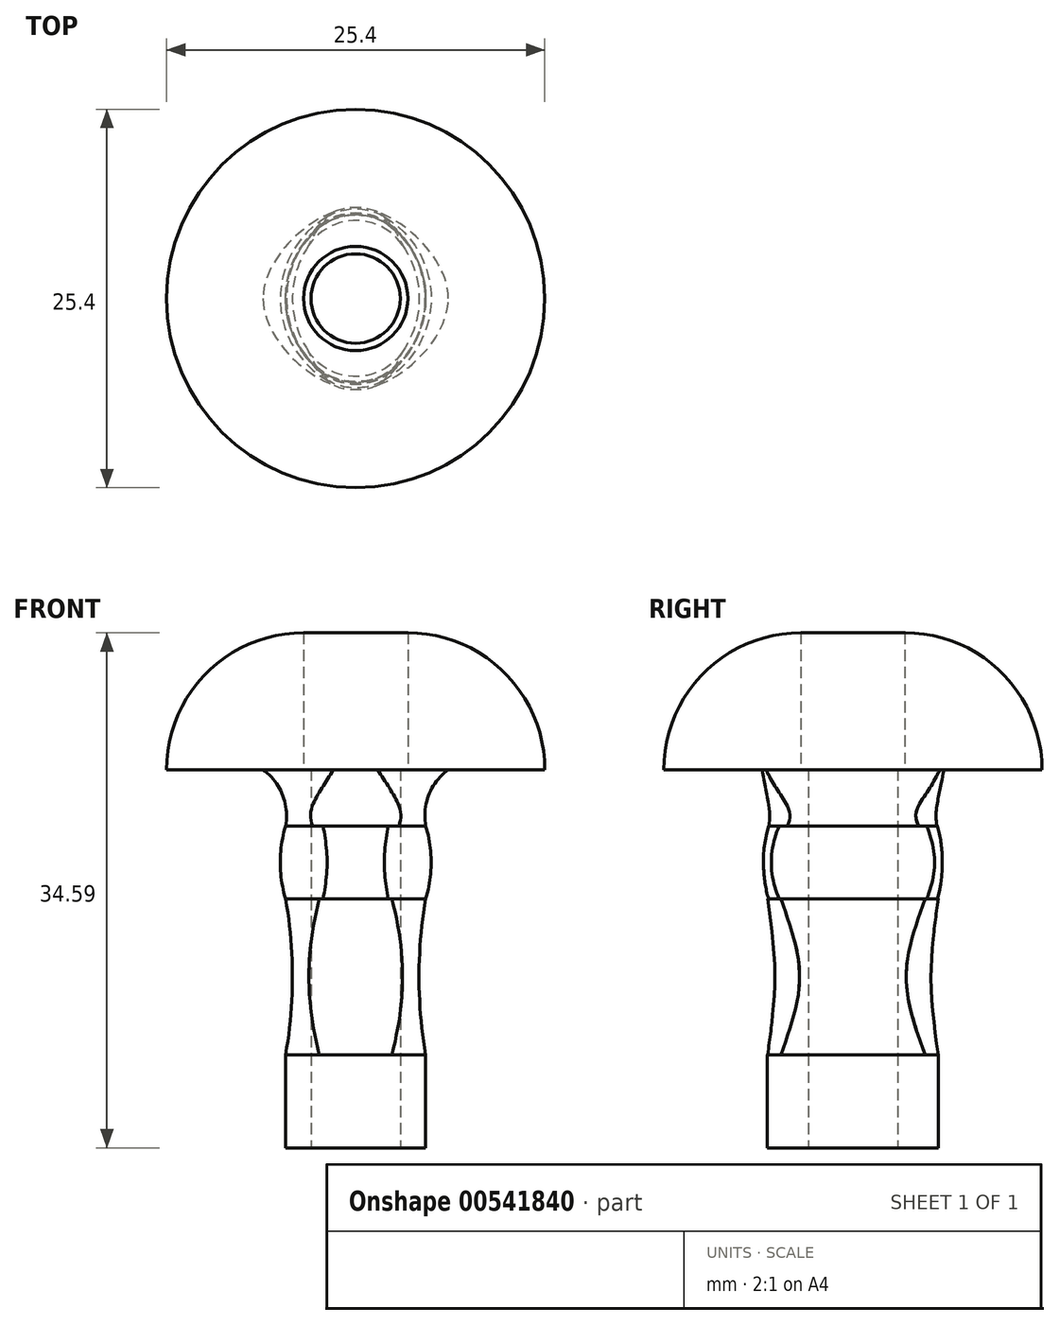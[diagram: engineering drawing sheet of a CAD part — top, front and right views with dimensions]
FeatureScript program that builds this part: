
annotation { "Feature Type Name" : "Feature", "Feature Type Description" : "" }
export const myFeature = defineFeature(function(context is Context, id is Id, definition is map)
    precondition{}
    {
        {
            var Q0;
            Q0=qCreatedBy(makeId("Front.planeOp"),FACE);
            var sketch = newSketch(context, id + "F0", { "sketchPlane" : qUnion([Q0])});
            skArc(sketch, "E0", {"start": v(-4.7, 21.62) * mm, "mid": v(-4.92, 23.73) * mm, "end": v(-6.22, 25.4) * mm});
            skArc(sketch, "E1", {"start": v(-4.7, 21.62) * mm, "mid": v(-5.07, 19.17) * mm, "end": v(-4.7, 16.71) * mm});
            skArc(sketch, "E2", {"start": v(-4.7, 6.26) * mm, "mid": v(-4.25, 11.49) * mm, "end": v(-4.7, 16.71) * mm});
            skLineSegment(sketch, "E3", {"start": v(-4.7, 6.26) * mm, "end": v(-3.92, 6.26) * mm});
            skLineSegment(sketch, "E4.MirrorCS", {"start": v(4.7, 6.26) * mm, "end": v(3.92, 6.26) * mm});
            skArc(sketch, "E5.MirrorCS", {"start": v(4.7, 6.26) * mm, "mid": v(4.25, 11.49) * mm, "end": v(4.7, 16.71) * mm});
            skArc(sketch, "E6.MirrorCS", {"start": v(4.7, 21.62) * mm, "mid": v(5.07, 19.17) * mm, "end": v(4.7, 16.71) * mm});
            skArc(sketch, "E7.MirrorCS", {"start": v(4.7, 21.62) * mm, "mid": v(4.92, 23.73) * mm, "end": v(6.22, 25.4) * mm});
            skLineSegment(sketch, "E8", {"start": v(-6.22, 25.4) * mm, "end": v(6.22, 25.4) * mm});
            skLineSegment(sketch, "E9", {"start": v(-4.7, 21.62) * mm, "end": v(4.7, 21.62) * mm});
            skLineSegment(sketch, "E10", {"start": v(-4.7, 16.71) * mm, "end": v(4.7, 16.71) * mm});
            skLineSegment(sketch, "E11", {"start": v(-3.92, 6.26) * mm, "end": v(3.92, 6.26) * mm});
            skLineSegment(sketch, "E12", {"start": v(-4.7, 6.26) * mm, "end": v(-4.7, 0) * mm});
            skLineSegment(sketch, "E13", {"start": v(-4.7, 0) * mm, "end": v(3.39, 0) * mm});
            skLineSegment(sketch, "E14", {"start": v(4.7, 6.26) * mm, "end": v(4.7, 0) * mm});
            skLineSegment(sketch, "E15", {"start": v(4.7, 0) * mm, "end": v(3.39, 0) * mm});
            skSolve(sketch);
        }
        {
            var Q0;
            Q0=qCreatedBy(makeId("Top.planeOp"),FACE);
            var sketch = newSketch(context, id + "F1", { "sketchPlane" : qUnion([Q0])});
            skCircle(sketch, "E16", {"center": v(0, 0) * mm, "radius": 3.5 * mm});
            skCircle(sketch, "E17", {"center": v(0, 0) * mm, "radius": 12.7 * mm});
            skSolve(sketch);
        }
        {
            var Q0;
            Q0=makeQuery(id+"F1.imprint","IMPRINT",FACE,{"disambiguationData":[TD([[makeQuery(id+"F1.imprint","IMPRINT",EDGE,{"derivedFrom":sQuery(id+"F1.wireOp",EDGE,"E16")}),-1.0]])]});
            extrude(context, id + "F2", {"entities" : qUnion([Q0]), "depth" : 9.2 * mm, "offsetDistance" : 25.4 * mm});
        }
        {
            var Q0;
            Q0=makeQuery(id+"F2.opExtrude","SWEPT_BODY",BODY,{"disambiguationData":[OSD([sQuery(id+"F1.wireOp",EDGE,"E16"),sQuery(id+"F1.wireOp",EDGE,"PXPxztUf-wTVu-soCt-rwad-Ievf1r8iTORp.bottom"),sQuery(id+"F1.wireOp",EDGE,"PXPxztUf-wTVu-soCt-rwad-Ievf1r8iTORp.top"),sQuery(id+"F1.wireOp",EDGE,"PXPxztUf-wTVu-soCt-rwad-Ievf1r8iTORp.left"),sQuery(id+"F1.wireOp",EDGE,"PXPxztUf-wTVu-soCt-rwad-Ievf1r8iTORp.right")])]});
            transform(context, id + "F3", {"entities" : qUnion([Q0]), "transformType" : TransformType.TRANSLATION_3D, "dx" : 0 * mm, "dy" : 0 * mm, "dz" : 25.4 * mm, "makeCopy" : false});
        }
        {
            var Q0;
            Q0=makeQuery(id+"F2.opExtrude","CAP_EDGE",EDGE,{"disambiguationData":[OSD([sQuery(id+"F1.wireOp",EDGE,"E17")])],"isStart":false});
            fillet(context, id + "F4", {"entities" : qUnion([Q0]), "radius" : 9.2 * mm, "tangentPropagation" : true, "allowEdgeOverflow" : false});
        }
        {
            var Q0;
            Q0=makeQuery(id+"F0.imprint","IMPRINT",FACE,{"disambiguationData":[TD([[makeQuery(id+"F0.imprint","IMPRINT",EDGE,{"derivedFrom":sQuery(id+"F0.wireOp",EDGE,"E2")}),-1.0]])]});
            extrude(context, id + "F5", {"entities" : qUnion([Q0]), "depth" : 12.7 * mm, "offsetDistance" : 25.4 * mm});
        }
        {
            var Q0;
            Q0=makeQuery(id+"F5.opExtrude","SWEPT_BODY",BODY,{"disambiguationData":[OSD([sQuery(id+"F0.wireOp",EDGE,"E2"),sQuery(id+"F0.wireOp",EDGE,"E3"),sQuery(id+"F0.wireOp",EDGE,"E4.MirrorCS"),sQuery(id+"F0.wireOp",EDGE,"E5.MirrorCS"),sQuery(id+"F0.wireOp",EDGE,"E10"),sQuery(id+"F0.wireOp",EDGE,"E11")])]});
            transform(context, id + "F6", {"entities" : qUnion([Q0]), "transformType" : TransformType.TRANSLATION_3D, "dx" : 0 * mm, "dy" : 6.35 * mm, "dz" : 0 * mm, "makeCopy" : false});
        }
        {
            var Q0;
            Q0=makeQuery(id+"F5.opExtrude","CAP_EDGE",EDGE,{"disambiguationData":[OSD([sQuery(id+"F0.wireOp",EDGE,"E5.MirrorCS")])],"isStart":false});
            var Q1;
            Q1=makeQuery(id+"F5.opExtrude","CAP_EDGE",EDGE,{"disambiguationData":[OSD([sQuery(id+"F0.wireOp",EDGE,"E2")])],"isStart":false});
            var Q2;
            Q2=makeQuery(id+"F5.opExtrude","CAP_EDGE",EDGE,{"disambiguationData":[OSD([sQuery(id+"F0.wireOp",EDGE,"E5.MirrorCS")])],"isStart":true});
            var Q3;
            Q3=makeQuery(id+"F5.opExtrude","CAP_EDGE",EDGE,{"disambiguationData":[OSD([sQuery(id+"F0.wireOp",EDGE,"E2")])],"isStart":true});
            fillet(context, id + "F7", {"entities" : qUnion([Q0, Q1, Q2, Q3]), "radius" : 6.35 * mm, "tangentPropagation" : true, "allowEdgeOverflow" : false});
        }
        {
            var Q0;
            Q0=makeQuery(id+"F0.imprint","IMPRINT",FACE,{"disambiguationData":[TD([[makeQuery(id+"F0.imprint","IMPRINT",EDGE,{"derivedFrom":sQuery(id+"F0.wireOp",EDGE,"E3")}),-1.0]])]});
            extrude(context, id + "F8", {"entities" : qUnion([Q0]), "depth" : 12.7 * mm, "offsetDistance" : 25.4 * mm});
        }
        {
            var Q0;
            Q0=makeQuery(id+"F8.opExtrude","SWEPT_BODY",BODY,{"disambiguationData":[OSD([sQuery(id+"F0.wireOp",EDGE,"E3"),sQuery(id+"F0.wireOp",EDGE,"E4.MirrorCS"),sQuery(id+"F0.wireOp",EDGE,"E11"),sQuery(id+"F0.wireOp",EDGE,"E12"),sQuery(id+"F0.wireOp",EDGE,"E13"),sQuery(id+"F0.wireOp",EDGE,"E14"),sQuery(id+"F0.wireOp",EDGE,"E15")])]});
            transform(context, id + "F9", {"entities" : qUnion([Q0]), "transformType" : TransformType.TRANSLATION_3D, "dx" : 0 * mm, "dy" : 6.35 * mm, "dz" : 0 * mm, "makeCopy" : false});
        }
        {
            var Q0;
            Q0=makeQuery(id+"F8.opExtrude","CAP_EDGE",EDGE,{"disambiguationData":[OSD([sQuery(id+"F0.wireOp",EDGE,"E14")])],"isStart":false});
            var Q1;
            Q1=makeQuery(id+"F8.opExtrude","CAP_EDGE",EDGE,{"disambiguationData":[OSD([sQuery(id+"F0.wireOp",EDGE,"E12")])],"isStart":false});
            var Q2;
            Q2=makeQuery(id+"F8.opExtrude","CAP_EDGE",EDGE,{"disambiguationData":[OSD([sQuery(id+"F0.wireOp",EDGE,"E14")])],"isStart":true});
            var Q3;
            Q3=makeQuery(id+"F8.opExtrude","CAP_EDGE",EDGE,{"disambiguationData":[OSD([sQuery(id+"F0.wireOp",EDGE,"E12")])],"isStart":true});
            fillet(context, id + "F10", {"entities" : qUnion([Q0, Q1, Q2, Q3]), "radius" : 6.35 * mm, "tangentPropagation" : true, "allowEdgeOverflow" : false});
        }
        {
            var Q0;
            Q0=makeQuery(id+"F0.imprint","IMPRINT",FACE,{"disambiguationData":[TD([[makeQuery(id+"F0.imprint","IMPRINT",EDGE,{"derivedFrom":sQuery(id+"F0.wireOp",EDGE,"E1")}),1.0]])]});
            extrude(context, id + "F11", {"entities" : qUnion([Q0]), "depth" : 12.7 * mm, "offsetDistance" : 25.4 * mm});
        }
        {
            var Q0;
            Q0=makeQuery(id+"F11.opExtrude","SWEPT_BODY",BODY,{"disambiguationData":[OSD([sQuery(id+"F0.wireOp",EDGE,"E1"),sQuery(id+"F0.wireOp",EDGE,"E6.MirrorCS"),sQuery(id+"F0.wireOp",EDGE,"E9"),sQuery(id+"F0.wireOp",EDGE,"E10")])]});
            transform(context, id + "F12", {"entities" : qUnion([Q0]), "transformType" : TransformType.TRANSLATION_3D, "dx" : 0 * mm, "dy" : 6.35 * mm, "dz" : 0 * mm, "makeCopy" : false});
        }
        {
            var Q0;
            Q0=makeQuery(id+"F11.opExtrude","CAP_EDGE",EDGE,{"disambiguationData":[OSD([sQuery(id+"F0.wireOp",EDGE,"E6.MirrorCS")])],"isStart":false});
            var Q1;
            Q1=makeQuery(id+"F11.opExtrude","CAP_EDGE",EDGE,{"disambiguationData":[OSD([sQuery(id+"F0.wireOp",EDGE,"E1")])],"isStart":false});
            var Q2;
            Q2=makeQuery(id+"F11.opExtrude","CAP_EDGE",EDGE,{"disambiguationData":[OSD([sQuery(id+"F0.wireOp",EDGE,"E6.MirrorCS")])],"isStart":true});
            var Q3;
            Q3=makeQuery(id+"F11.opExtrude","CAP_EDGE",EDGE,{"disambiguationData":[OSD([sQuery(id+"F0.wireOp",EDGE,"E1")])],"isStart":true});
            fillet(context, id + "F13", {"entities" : qUnion([Q0, Q1, Q2, Q3]), "radius" : 6.35 * mm, "tangentPropagation" : true, "allowEdgeOverflow" : false});
        }
        {
            var Q0;
            Q0=makeQuery(id+"F0.imprint","IMPRINT",FACE,{"disambiguationData":[TD([[makeQuery(id+"F0.imprint","IMPRINT",EDGE,{"derivedFrom":sQuery(id+"F0.wireOp",EDGE,"E0")}),-1.0]])]});
            extrude(context, id + "F14", {"entities" : qUnion([Q0]), "depth" : 12.7 * mm, "offsetDistance" : 25.4 * mm});
        }
        {
            var Q0;
            Q0=makeQuery(id+"F14.opExtrude","SWEPT_BODY",BODY,{"disambiguationData":[OSD([sQuery(id+"F0.wireOp",EDGE,"E0"),sQuery(id+"F0.wireOp",EDGE,"E7.MirrorCS"),sQuery(id+"F0.wireOp",EDGE,"E8"),sQuery(id+"F0.wireOp",EDGE,"E9")])]});
            transform(context, id + "F15", {"entities" : qUnion([Q0]), "transformType" : TransformType.TRANSLATION_3D, "dx" : 0 * mm, "dy" : 6.35 * mm, "dz" : 0 * mm, "makeCopy" : false});
        }
        {
            var Q0;
            Q0=makeQuery(id+"F14.opExtrude","CAP_EDGE",EDGE,{"disambiguationData":[OSD([sQuery(id+"F0.wireOp",EDGE,"E0")])],"isStart":false});
            var Q1;
            Q1=makeQuery(id+"F14.opExtrude","CAP_EDGE",EDGE,{"disambiguationData":[OSD([sQuery(id+"F0.wireOp",EDGE,"E7.MirrorCS")])],"isStart":false});
            var Q2;
            Q2=makeQuery(id+"F14.opExtrude","CAP_EDGE",EDGE,{"disambiguationData":[OSD([sQuery(id+"F0.wireOp",EDGE,"E7.MirrorCS")])],"isStart":true});
            var Q3;
            Q3=makeQuery(id+"F14.opExtrude","CAP_EDGE",EDGE,{"disambiguationData":[OSD([sQuery(id+"F0.wireOp",EDGE,"E0")])],"isStart":true});
            fillet(context, id + "F16", {"entities" : qUnion([Q0, Q1, Q2, Q3]), "radius" : 6.35 * mm, "tangentPropagation" : true, "allowEdgeOverflow" : false});
        }
        {
            var Q0;
            Q0=makeQuery(id+"F7.opFillet","BLEND_EDGE",EDGE,{"blendedFrom":[makeQuery(id+"F5.opExtrude","CAP_EDGE",EDGE,{"disambiguationData":[OSD([sQuery(id+"F0.wireOp",EDGE,"E2")])],"isStart":false}),makeQuery(id+"F5.opExtrude","CAP_EDGE",EDGE,{"disambiguationData":[OSD([sQuery(id+"F0.wireOp",EDGE,"E5.MirrorCS")])],"isStart":false})],"blendedInto":[]});
            var Q1;
            Q1=makeQuery(id+"F7.opFillet","BLEND_EDGE",EDGE,{"blendedFrom":[makeQuery(id+"F5.opExtrude","CAP_EDGE",EDGE,{"disambiguationData":[OSD([sQuery(id+"F0.wireOp",EDGE,"E2")])],"isStart":true}),makeQuery(id+"F5.opExtrude","CAP_EDGE",EDGE,{"disambiguationData":[OSD([sQuery(id+"F0.wireOp",EDGE,"E5.MirrorCS")])],"isStart":true})],"blendedInto":[]});
            fillet(context, id + "F17", {"entities" : qUnion([Q0, Q1]), "radius" : 3.8 * mm, "tangentPropagation" : true, "allowEdgeOverflow" : false});
        }
        {
            var Q0;
            Q0=makeQuery(id+"F10.opFillet","BLEND_EDGE",EDGE,{"blendedFrom":[makeQuery(id+"F8.opExtrude","CAP_EDGE",EDGE,{"disambiguationData":[OSD([sQuery(id+"F0.wireOp",EDGE,"E12")])],"isStart":false}),makeQuery(id+"F8.opExtrude","CAP_EDGE",EDGE,{"disambiguationData":[OSD([sQuery(id+"F0.wireOp",EDGE,"E14")])],"isStart":false})],"blendedInto":[]});
            var Q1;
            Q1=makeQuery(id+"F10.opFillet","BLEND_EDGE",EDGE,{"blendedFrom":[makeQuery(id+"F8.opExtrude","CAP_EDGE",EDGE,{"disambiguationData":[OSD([sQuery(id+"F0.wireOp",EDGE,"E12")])],"isStart":true}),makeQuery(id+"F8.opExtrude","CAP_EDGE",EDGE,{"disambiguationData":[OSD([sQuery(id+"F0.wireOp",EDGE,"E14")])],"isStart":true})],"blendedInto":[]});
            fillet(context, id + "F18", {"entities" : qUnion([Q0, Q1]), "radius" : 3.8 * mm, "tangentPropagation" : true, "allowEdgeOverflow" : false});
        }
        {
            var Q0;
            Q0=makeQuery(id+"F13.opFillet","BLEND_EDGE",EDGE,{"blendedFrom":[makeQuery(id+"F11.opExtrude","CAP_EDGE",EDGE,{"disambiguationData":[OSD([sQuery(id+"F0.wireOp",EDGE,"E1")])],"isStart":false}),makeQuery(id+"F11.opExtrude","CAP_EDGE",EDGE,{"disambiguationData":[OSD([sQuery(id+"F0.wireOp",EDGE,"E6.MirrorCS")])],"isStart":false})],"blendedInto":[]});
            var Q1;
            Q1=makeQuery(id+"F13.opFillet","BLEND_EDGE",EDGE,{"blendedFrom":[makeQuery(id+"F11.opExtrude","CAP_EDGE",EDGE,{"disambiguationData":[OSD([sQuery(id+"F0.wireOp",EDGE,"E1")])],"isStart":true}),makeQuery(id+"F11.opExtrude","CAP_EDGE",EDGE,{"disambiguationData":[OSD([sQuery(id+"F0.wireOp",EDGE,"E6.MirrorCS")])],"isStart":true})],"blendedInto":[]});
            fillet(context, id + "F19", {"entities" : qUnion([Q0, Q1]), "radius" : 3.8 * mm, "tangentPropagation" : true, "allowEdgeOverflow" : false});
        }
        {
            var Q0;
            Q0=makeQuery(id+"F16.opFillet","BLEND_EDGE",EDGE,{"blendedFrom":[makeQuery(id+"F14.opExtrude","CAP_EDGE",EDGE,{"disambiguationData":[OSD([sQuery(id+"F0.wireOp",EDGE,"E0")])],"isStart":false}),makeQuery(id+"F14.opExtrude","CAP_EDGE",EDGE,{"disambiguationData":[OSD([sQuery(id+"F0.wireOp",EDGE,"E7.MirrorCS")])],"isStart":false})],"blendedInto":[]});
            var Q1;
            Q1=makeQuery(id+"F16.opFillet","BLEND_EDGE",EDGE,{"blendedFrom":[makeQuery(id+"F14.opExtrude","CAP_EDGE",EDGE,{"disambiguationData":[OSD([sQuery(id+"F0.wireOp",EDGE,"E0")])],"isStart":true}),makeQuery(id+"F14.opExtrude","CAP_EDGE",EDGE,{"disambiguationData":[OSD([sQuery(id+"F0.wireOp",EDGE,"E7.MirrorCS")])],"isStart":true})],"blendedInto":[]});
            fillet(context, id + "F20", {"entities" : qUnion([Q0, Q1]), "radius" : 4.06 * mm, "tangentPropagation" : true, "allowEdgeOverflow" : false});
        }
        {
            var Q0;
            Q0=sQuery(id+"F1.wireOp",VERTEX,"E16.center");
            var Q1;
            Q1=makeQuery(id+"F5.opExtrude","SWEPT_BODY",BODY,{"disambiguationData":[OSD([sQuery(id+"F0.wireOp",EDGE,"E2"),sQuery(id+"F0.wireOp",EDGE,"E3"),sQuery(id+"F0.wireOp",EDGE,"E4.MirrorCS"),sQuery(id+"F0.wireOp",EDGE,"E5.MirrorCS"),sQuery(id+"F0.wireOp",EDGE,"E10"),sQuery(id+"F0.wireOp",EDGE,"E11")])]});
            var Q2;
            Q2=makeQuery(id+"F8.opExtrude","SWEPT_BODY",BODY,{"disambiguationData":[OSD([sQuery(id+"F0.wireOp",EDGE,"E3"),sQuery(id+"F0.wireOp",EDGE,"E4.MirrorCS"),sQuery(id+"F0.wireOp",EDGE,"E11"),sQuery(id+"F0.wireOp",EDGE,"E12"),sQuery(id+"F0.wireOp",EDGE,"E13"),sQuery(id+"F0.wireOp",EDGE,"E14"),sQuery(id+"F0.wireOp",EDGE,"E15")])]});
            var Q3;
            Q3=makeQuery(id+"F11.opExtrude","SWEPT_BODY",BODY,{"disambiguationData":[OSD([sQuery(id+"F0.wireOp",EDGE,"E1"),sQuery(id+"F0.wireOp",EDGE,"E6.MirrorCS"),sQuery(id+"F0.wireOp",EDGE,"E9"),sQuery(id+"F0.wireOp",EDGE,"E10")])]});
            var Q4;
            Q4=makeQuery(id+"F14.opExtrude","SWEPT_BODY",BODY,{"disambiguationData":[OSD([sQuery(id+"F0.wireOp",EDGE,"E0"),sQuery(id+"F0.wireOp",EDGE,"E7.MirrorCS"),sQuery(id+"F0.wireOp",EDGE,"E8"),sQuery(id+"F0.wireOp",EDGE,"E9")])]});
            hole(context, id + "F21", {"style" : HoleStyle.SIMPLE, "endStyle" : HoleEndStyle.THROUGH, "oppositeDirection" : true, "holeDiameter" : 6 * mm, "isTappedThrough" : true, "tappedDepth" : 12.7 * mm, "tapClearance" : 3, "locations" : qUnion([Q0]), "scope" : qUnion([Q1, Q2, Q3, Q4])});
        }
    });
